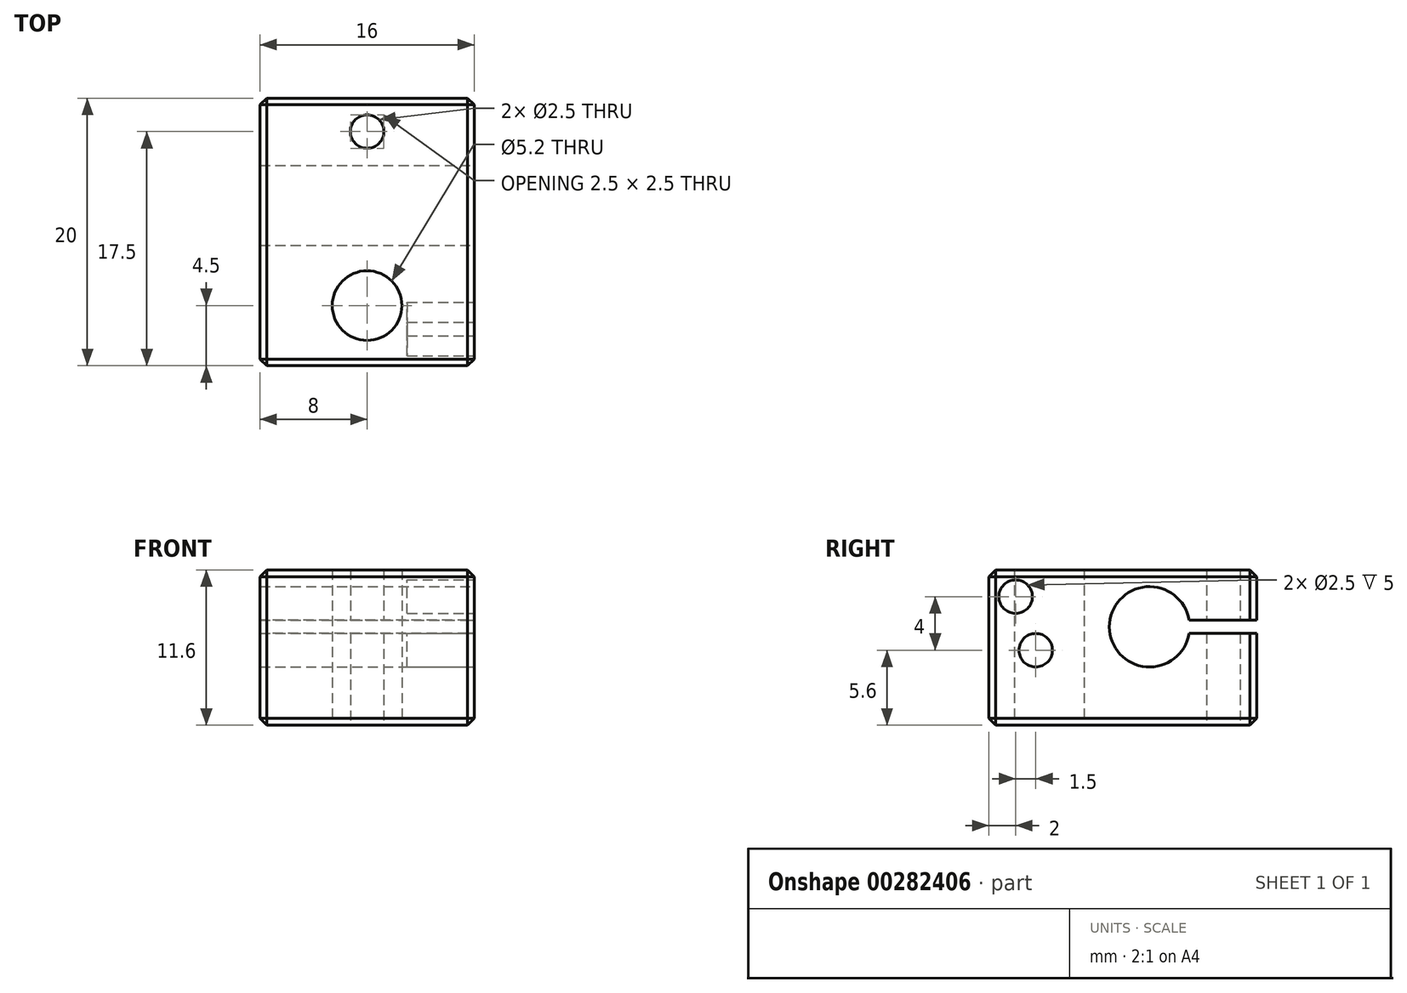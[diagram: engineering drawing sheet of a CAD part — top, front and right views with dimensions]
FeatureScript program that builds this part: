
annotation { "Feature Type Name" : "Feature", "Feature Type Description" : "" }
export const myFeature = defineFeature(function(context is Context, id is Id, definition is map)
    precondition{}
    {
        {
            var Q0;
            Q0=qCreatedBy(makeId("Top.planeOp"),FACE);
            var sketch = newSketch(context, id + "F0", { "sketchPlane" : qUnion([Q0])});
            skLineSegment(sketch, "E0.bottom", {"start": v(0, 0) * mm, "end": v(16, 0) * mm});
            skLineSegment(sketch, "E0.top", {"start": v(0, 20) * mm, "end": v(16, 20) * mm});
            skLineSegment(sketch, "E0.left", {"start": v(0, 0) * mm, "end": v(0, 20) * mm});
            skLineSegment(sketch, "E0.right", {"start": v(16, 0) * mm, "end": v(16, 20) * mm});
            skCircle(sketch, "E1", {"center": v(8, 4.5) * mm, "radius": 2.6 * mm});
            skCircle(sketch, "E2", {"center": v(8, 17.5) * mm, "radius": 1.25 * mm});
            skSolve(sketch);
        }
        {
            var Q0;
            Q0=qSketchRegion(id+"F0",true);
            extrude(context, id + "F1", {"entities" : qUnion([Q0]), "depth" : 11.6 * mm});
        }
        {
            var Q0;
            Q0=makeQuery(id+"F1.opExtrude","SWEPT_FACE",FACE,{"disambiguationData":[OSD([sQuery(id+"F0.wireOp",EDGE,"E0.right")])]});
            var sketch = newSketch(context, id + "F2", { "sketchPlane" : qUnion([Q0])});
            skArc(sketch, "E3", {"start": v(14.96, 7.85) * mm, "mid": v(9, 7.35) * mm, "end": v(14.96, 6.85) * mm});
            skLineSegment(sketch, "E4", {"start": v(12, 7.35) * mm, "end": v(20, 7.35) * mm, "construction": true});
            skLineSegment(sketch, "E5.0", {"start": v(14.96, 6.85) * mm, "end": v(21.96, 6.85) * mm});
            skLineSegment(sketch, "E6.0", {"start": v(14.96, 7.85) * mm, "end": v(21.96, 7.85) * mm});
            skLineSegment(sketch, "E7", {"start": v(21.96, 7.85) * mm, "end": v(21.96, 6.85) * mm});
            skSolve(sketch);
        }
        {
            var Q0;
            Q0=qSketchRegion(id+"F2",true);
            extrude(context, id + "F3", {"entities" : qUnion([Q0]), "operationType" : NewBodyOperationType.REMOVE, "endBound" : BoundingType.THROUGH_ALL, "oppositeDirection" : true, "depth" : 25 * mm});
        }
        {
            var Q0;
            Q0=makeQuery(id+"F1.opExtrude","SWEPT_FACE",FACE,{"disambiguationData":[OSD([sQuery(id+"F0.wireOp",EDGE,"E0.right")])]});
            var sketch = newSketch(context, id + "F4", { "sketchPlane" : qUnion([Q0])});
            skCircle(sketch, "E8", {"center": v(2, 9.6) * mm, "radius": 1.25 * mm});
            skCircle(sketch, "E9", {"center": v(3.5, 5.6) * mm, "radius": 1.25 * mm});
            skSolve(sketch);
        }
        {
            var Q0;
            Q0=qSketchRegion(id+"F4",true);
            extrude(context, id + "F5", {"entities" : qUnion([Q0]), "operationType" : NewBodyOperationType.REMOVE, "oppositeDirection" : true, "depth" : 5 * mm});
        }
        {
            var Q0;
            Q0=makeQuery(id+"F1.opExtrude","SWEPT_FACE",FACE,{"disambiguationData":[OSD([sQuery(id+"F0.wireOp",EDGE,"E0.bottom")])]});
            var Q1;
            Q1=makeQuery(id+"F1.opExtrude","CAP_EDGE",EDGE,{"disambiguationData":[OSD([sQuery(id+"F0.wireOp",EDGE,"E0.right")])],"isStart":false});
            var Q2;
            Q2=makeQuery(id+"F1.opExtrude","CAP_EDGE",EDGE,{"disambiguationData":[OSD([sQuery(id+"F0.wireOp",EDGE,"E0.right")])],"isStart":true});
            var Q3;
            {var subQ0=sQuery(id+"F0.wireOp",EDGE,"E0.right");var subQ1=sQuery(id+"F0.wireOp",EDGE,"E0.top");Q3=makeQuery(id+"F3.boolean.opBoolean","SPLIT",EDGE,{"disambiguationData":[TD([makeQuery(id+"F3.opExtrude","SWEPT_FACE",FACE,{"disambiguationData":[OSD([sQuery(id+"F2.wireOp",EDGE,"E5.0")])]})])],"derivedFrom":makeQuery(id+"F1.opExtrude","SWEPT_EDGE",EDGE,{"disambiguationData":[OSD([subQ1,subQ0])]})});}
            var Q4;
            {var subQ0=sQuery(id+"F0.wireOp",EDGE,"E0.right");var subQ1=sQuery(id+"F0.wireOp",EDGE,"E0.top");Q4=makeQuery(id+"F3.boolean.opBoolean","SPLIT",EDGE,{"disambiguationData":[TD([makeQuery(id+"F3.opExtrude","SWEPT_FACE",FACE,{"disambiguationData":[OSD([sQuery(id+"F2.wireOp",EDGE,"E6.0")])]})])],"derivedFrom":makeQuery(id+"F1.opExtrude","SWEPT_EDGE",EDGE,{"disambiguationData":[OSD([subQ1,subQ0])]})});}
            var Q5;
            {var subQ0=sQuery(id+"F0.wireOp",EDGE,"E0.left");var subQ1=sQuery(id+"F0.wireOp",EDGE,"E0.top");Q5=makeQuery(id+"F3.boolean.opBoolean","SPLIT",EDGE,{"disambiguationData":[TD([makeQuery(id+"F3.opExtrude","SWEPT_FACE",FACE,{"disambiguationData":[OSD([sQuery(id+"F2.wireOp",EDGE,"E6.0")])]})])],"derivedFrom":makeQuery(id+"F1.opExtrude","SWEPT_EDGE",EDGE,{"disambiguationData":[OSD([subQ1,subQ0])]})});}
            var Q6;
            Q6=makeQuery(id+"F1.opExtrude","CAP_EDGE",EDGE,{"disambiguationData":[OSD([sQuery(id+"F0.wireOp",EDGE,"E0.top")])],"isStart":false});
            var Q7;
            Q7=makeQuery(id+"F1.opExtrude","CAP_EDGE",EDGE,{"disambiguationData":[OSD([sQuery(id+"F0.wireOp",EDGE,"E0.top")])],"isStart":true});
            var Q8;
            {var subQ0=sQuery(id+"F0.wireOp",EDGE,"E0.left");var subQ1=sQuery(id+"F0.wireOp",EDGE,"E0.top");Q8=makeQuery(id+"F3.boolean.opBoolean","SPLIT",EDGE,{"disambiguationData":[TD([makeQuery(id+"F3.opExtrude","SWEPT_FACE",FACE,{"disambiguationData":[OSD([sQuery(id+"F2.wireOp",EDGE,"E5.0")])]})])],"derivedFrom":makeQuery(id+"F1.opExtrude","SWEPT_EDGE",EDGE,{"disambiguationData":[OSD([subQ1,subQ0])]})});}
            var Q9;
            Q9=makeQuery(id+"F1.opExtrude","CAP_EDGE",EDGE,{"disambiguationData":[OSD([sQuery(id+"F0.wireOp",EDGE,"E0.left")])],"isStart":false});
            var Q10;
            Q10=makeQuery(id+"F1.opExtrude","CAP_EDGE",EDGE,{"disambiguationData":[OSD([sQuery(id+"F0.wireOp",EDGE,"E0.left")])],"isStart":true});
            chamfer(context, id + "F6", {"entities" : qUnion([Q0, Q1, Q2, Q3, Q4, Q5, Q6, Q7, Q8, Q9, Q10]), "width" : 0.5 * mm, "tangentPropagation" : true});
        }
    });
